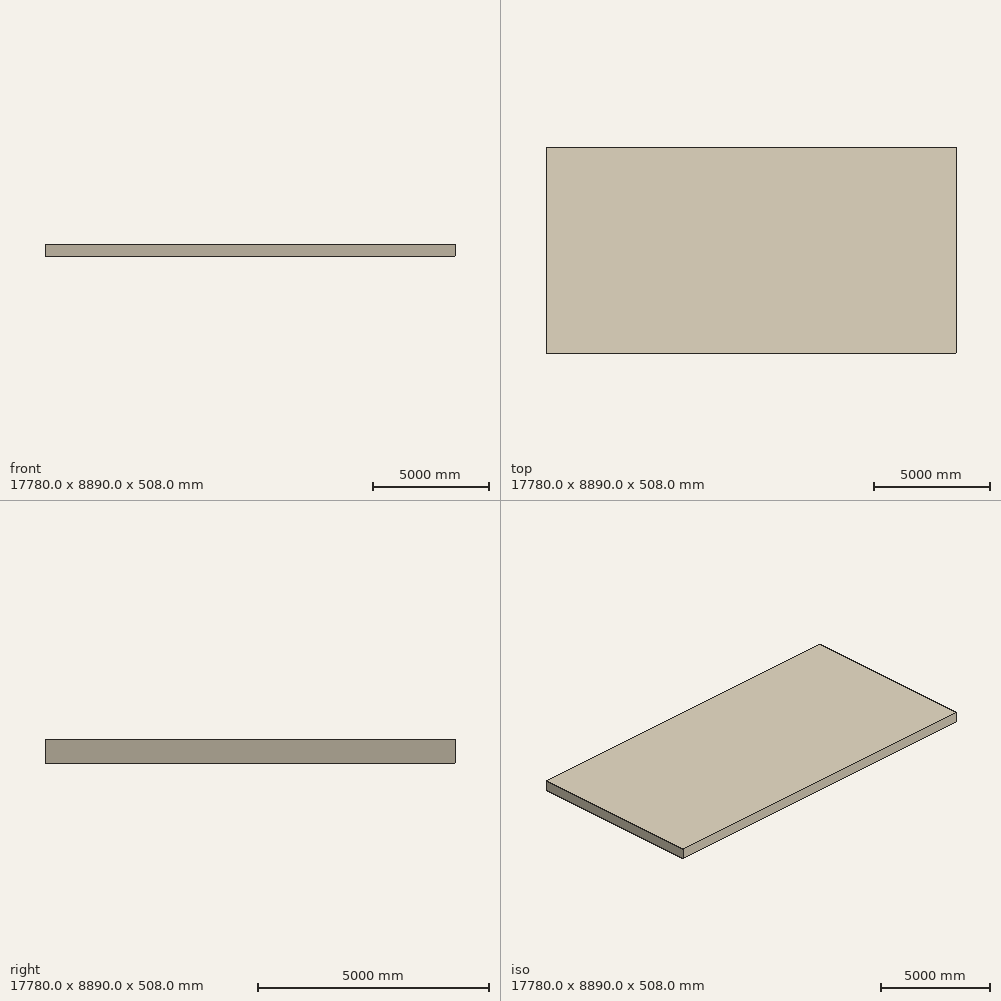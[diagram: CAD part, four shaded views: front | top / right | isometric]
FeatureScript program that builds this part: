
annotation { "Feature Type Name" : "Feature", "Feature Type Description" : "" }
export const myFeature = defineFeature(function(context is Context, id is Id, definition is map)
    precondition{}
    {
        {
            var Q0;
            Q0=qCreatedBy(makeId("Top.planeOp"),FACE);
            var sketch = newSketch(context, id + "F0", { "sketchPlane" : qUnion([Q0])});
            skLineSegment(sketch, "E0", {"start": v(-8890, 4445) * mm, "end": v(-8890, -4445) * mm});
            skLineSegment(sketch, "E1", {"start": v(-8890, -4445) * mm, "end": v(8890, -4445) * mm});
            skLineSegment(sketch, "E2", {"start": v(8890, -4445) * mm, "end": v(8890, 4445) * mm});
            skLineSegment(sketch, "E3", {"start": v(8890, 4445) * mm, "end": v(-8890, 4445) * mm});
            skSolve(sketch);
        }
        {
            var Q0;
            Q0=makeQuery(id+"F0.imprint","IMPRINT",FACE,{"disambiguationData":[TD([[makeQuery(id+"F0.imprint","IMPRINT",EDGE,{"derivedFrom":sQuery(id+"F0.wireOp",EDGE,"E0")}),1.0]])]});
            extrude(context, id + "F1", {"entities" : qUnion([Q0]), "depth" : 508 * mm, "offsetDistance" : 25.4 * mm});
        }
    });
